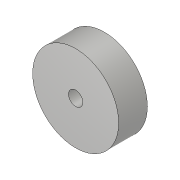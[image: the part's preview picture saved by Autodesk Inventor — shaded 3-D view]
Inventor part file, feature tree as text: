
AUTODESK INVENTOR PART (.ipt)
format: ipt  version: 2018.3 (Build 223284000, 284)  size: 84,480 bytes
history: native  units: in
note: dims shown in document units (in); Inventor stores cm internally (conversion verified against a paired STEP export)
features: extrude x1, sketch x1
ambient origin geometry x8: Origin, YZ Plane, XZ Plane, XY Plane, X Axis, Y Axis, Z Axis, Center Point
bodies: Solid1 (feature_tree)
feature tree (2):
  extrude  "Extrusion1"  Depth=0.25in
  sketch  "Sketch1"  dims[d0=0.125in d1=0.75in d2=0.25in d3=0.0in]
